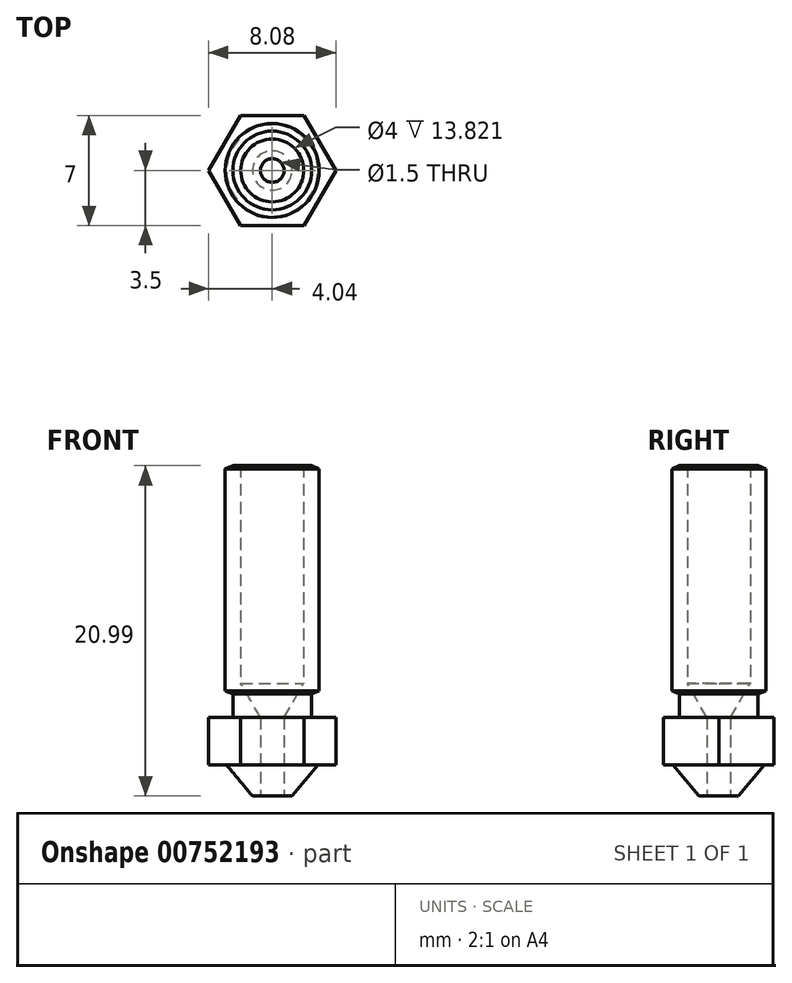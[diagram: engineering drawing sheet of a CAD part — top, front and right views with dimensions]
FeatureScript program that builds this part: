
annotation { "Feature Type Name" : "Feature", "Feature Type Description" : "" }
export const myFeature = defineFeature(function(context is Context, id is Id, definition is map)
    precondition{}
    {
        {
            var Q0;
            Q0=qCreatedBy(makeId("Front.planeOp"),FACE);
            var sketch = newSketch(context, id + "F0", { "sketchPlane" : qUnion([Q0])});
            skCircle(sketch, "E0.cCircle", {"center": v(-22.17, -14.6) * mm, "radius": 3.5 * mm, "construction": true});
            skLineSegment(sketch, "E0.0", {"start": v(-24.2, -11.1) * mm, "end": v(-20.15, -11.1) * mm});
            skLineSegment(sketch, "E0.1", {"start": v(-20.15, -11.1) * mm, "end": v(-18.13, -14.6) * mm});
            skLineSegment(sketch, "E0.2", {"start": v(-18.13, -14.6) * mm, "end": v(-20.15, -18.1) * mm});
            skLineSegment(sketch, "E0.3", {"start": v(-20.15, -18.1) * mm, "end": v(-24.2, -18.1) * mm});
            skLineSegment(sketch, "E0.4", {"start": v(-24.2, -18.1) * mm, "end": v(-26.21, -14.6) * mm});
            skLineSegment(sketch, "E0.5", {"start": v(-26.21, -14.6) * mm, "end": v(-24.2, -11.1) * mm});
            skPoint(sketch, "E0.0.midPoint", {"position": v(-22.17, -11.1) * mm});
            skLineSegment(sketch, "E1", {"start": v(-22.17, -11.1) * mm, "end": v(-22.17, -3.32) * mm});
            skLineSegment(sketch, "E2", {"start": v(-22.17, -7.82) * mm, "end": v(-18.13, -7.82) * mm});
            skLineSegment(sketch, "E3", {"start": v(-20.15, -11.1) * mm, "end": v(-20.15, -7.82) * mm, "construction": true});
            skLineSegment(sketch, "E4", {"start": v(-18.13, -7.82) * mm, "end": v(-18.13, -4.82) * mm});
            skLineSegment(sketch, "E5", {"start": v(-18.13, -4.82) * mm, "end": v(-22.17, -4.82) * mm});
            skLineSegment(sketch, "E6", {"start": v(-20.15, -7.82) * mm, "end": v(-20.15, -4.82) * mm});
            skLineSegment(sketch, "E7", {"start": v(-19.67, -4.82) * mm, "end": v(-19.67, -3.32) * mm});
            skLineSegment(sketch, "E8", {"start": v(-19.67, -3.32) * mm, "end": v(-22.17, -3.32) * mm, "construction": true});
            skLineSegment(sketch, "E9", {"start": v(-19.67, -3.32) * mm, "end": v(-19.19, -3.13) * mm});
            skLineSegment(sketch, "E10", {"start": v(-19.19, -3.13) * mm, "end": v(-19.19, 10.98) * mm});
            skLineSegment(sketch, "E11.0", {"start": v(-19.67, 11.18) * mm, "end": v(-22.17, 11.18) * mm});
            skLineSegment(sketch, "E12", {"start": v(-22.17, 11.18) * mm, "end": v(-22.17, 17.83) * mm});
            skLineSegment(sketch, "E13", {"start": v(-22.17, -3.32) * mm, "end": v(-22.17, 11.18) * mm});
            skLineSegment(sketch, "E14", {"start": v(-22.17, 3.93) * mm, "end": v(-16.93, 3.93) * mm, "construction": true});
            skLineSegment(sketch, "E15.MirrorCS", {"start": v(-19.67, 11.18) * mm, "end": v(-19.19, 10.98) * mm});
            skLineSegment(sketch, "E16", {"start": v(-19.19, -3.13) * mm, "end": v(-22.17, -3.13) * mm, "construction": true});
            skLineSegment(sketch, "E17", {"start": v(-19.19, 10.98) * mm, "end": v(-22.17, 10.98) * mm, "construction": true});
            skLineSegment(sketch, "E18", {"start": v(-20.17, 11.18) * mm, "end": v(-20.17, -2.64) * mm});
            skLineSegment(sketch, "E19", {"start": v(-22.17, -9.8) * mm, "end": v(-20.92, -9.8) * mm});
            skLineSegment(sketch, "E20", {"start": v(-20.92, -9.8) * mm, "end": v(-19.27, -7.82) * mm});
            skLineSegment(sketch, "E21", {"start": v(-21.42, -9.8) * mm, "end": v(-21.42, -4.8) * mm});
            skLineSegment(sketch, "E22", {"start": v(-21.42, -4.8) * mm, "end": v(-20.17, -2.64) * mm});
            skSolve(sketch);
        }
        {
            var Q0;
            {var subQ0=sQuery(id+"F0.wireOp",EDGE,"E7");Q0=makeQuery(id+"F0.imprint","IMPRINT",FACE,{"disambiguationData":[TD([[makeQuery(id+"F0.imprint","IMPRINT",EDGE,{"derivedFrom":subQ0}),1.0]])]});}
            var Q1;
            {var subQ0=sQuery(id+"F0.wireOp",EDGE,"E6");Q1=makeQuery(id+"F0.imprint","IMPRINT",FACE,{"disambiguationData":[TD([[makeQuery(id+"F0.imprint","IMPRINT",EDGE,{"derivedFrom":subQ0}),1.0]])]});}
            var Q2;
            {var subQ0=sQuery(id+"F0.wireOp",EDGE,"E20");Q2=makeQuery(id+"F0.imprint","IMPRINT",FACE,{"disambiguationData":[TD([[makeQuery(id+"F0.imprint","IMPRINT",EDGE,{"derivedFrom":subQ0}),1.0]])]});}
            var Q3;
            Q3=sQuery(id+"F0.wireOp",EDGE,"E12");
            revolve(context, id + "F1", {"surfaceOperationType" : NewSurfaceOperationType.NEW, "entities" : qUnion([Q0, Q1, Q2]), "axis" : qUnion([Q3]), "revolveType" : RevolveType.FULL});
        }
        {
            var Q0;
            Q0=makeQuery(id+"F1.opRevolve","SWEPT_FACE",FACE,{"disambiguationData":[OSD([sQuery(id+"F0.wireOp",EDGE,"E5")])]});
            var sketch = newSketch(context, id + "F2", { "sketchPlane" : qUnion([Q0])});
            skCircle(sketch, "E23.0.0", {"center": v(-22.17, 0) * mm, "radius": 2.5 * mm, "construction": true});
            skCircle(sketch, "E24.cCircle", {"center": v(-22.17, 0) * mm, "radius": 3.5 * mm, "construction": true});
            skLineSegment(sketch, "E24.0", {"start": v(-24.2, 3.5) * mm, "end": v(-20.15, 3.5) * mm});
            skLineSegment(sketch, "E24.1", {"start": v(-20.15, 3.5) * mm, "end": v(-18.13, 0) * mm});
            skLineSegment(sketch, "E24.2", {"start": v(-18.13, 0) * mm, "end": v(-20.15, -3.5) * mm});
            skLineSegment(sketch, "E24.3", {"start": v(-20.15, -3.5) * mm, "end": v(-24.2, -3.5) * mm});
            skLineSegment(sketch, "E24.4", {"start": v(-24.2, -3.5) * mm, "end": v(-26.21, 0) * mm});
            skLineSegment(sketch, "E24.5", {"start": v(-26.21, 0) * mm, "end": v(-24.2, 3.5) * mm});
            skPoint(sketch, "E24.0.midPoint", {"position": v(-22.17, 3.5) * mm});
            skSolve(sketch);
        }
        {
            var Q0;
            Q0=makeQuery(id+"F2.imprint","IMPRINT",FACE,{"disambiguationData":[TD([[makeQuery(id+"F2.imprint","IMPRINT",EDGE,{"derivedFrom":sQuery(id+"F2.wireOp",EDGE,"E24.0")}),-1.0]])]});
            var Q1;
            Q1=makeQuery(id+"F2.imprint","IMPRINT",FACE,{"disambiguationData":[TD([[makeQuery(id+"F2.imprint","IMPRINT",EDGE,{"derivedFrom":makeQuery(id+"F1.opRevolve","SWEPT_EDGE",EDGE,{"disambiguationData":[OSD([sQuery(id+"F0.wireOp",EDGE,"E5"),sQuery(id+"F0.wireOp",EDGE,"E7")])]})}),1.0]])]});
            var Q2;
            Q2=makeQuery(id+"F1.opRevolve","SWEPT_FACE",FACE,{"disambiguationData":[OSD([sQuery(id+"F0.wireOp",EDGE,"E2")])]});
            extrude(context, id + "F3", {"entities" : qUnion([Q0, Q1]), "operationType" : NewBodyOperationType.ADD, "endBound" : BoundingType.UP_TO_SURFACE, "depth" : 25 * mm, "endBoundEntityFace" : qUnion([Q2]), "offsetDistance" : 25 * mm});
        }
        {
            var Q0;
            Q0=makeQuery(id+"F1.opRevolve","SWEPT_BODY",BODY,{"disambiguationData":[OSD([sQuery(id+"F0.wireOp",EDGE,"E1"),sQuery(id+"F0.wireOp",EDGE,"xcYUQjN2-Zx3a-0UNT-urBn-dGCw2vRQanaT"),sQuery(id+"F0.wireOp",EDGE,"u3ff4xL9-JtKn-PGhM-6MFM-Q4x5irorrMbF"),sQuery(id+"F0.wireOp",EDGE,"E2")])]});
            var Q1;
            Q1=sQuery(id+"F0.wireOp",VERTEX,"E19.start");
            var Q2;
            Q2=qCreatedBy(makeId("Origin.pointOp"),VERTEX);
            transform(context, id + "F4", {"entities" : qUnion([Q0]), "transformType" : TransformType.TRANSLATION_ENTITY, "oppositeDirectionEntity" : false, "transformLine" : qUnion([Q1, Q2]), "makeCopy" : false});
        }
    });
